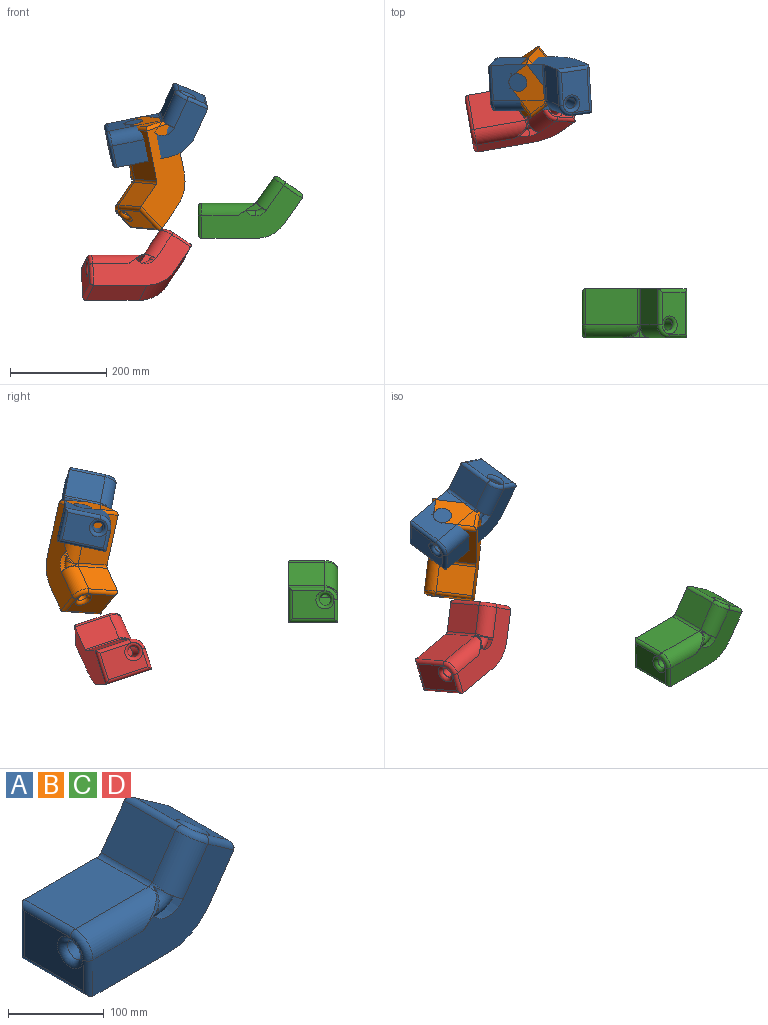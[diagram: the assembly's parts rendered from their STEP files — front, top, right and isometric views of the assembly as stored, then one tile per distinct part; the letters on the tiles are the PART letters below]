
ASSEMBLY  parts=4 mates=2
PART A: 31 faces, bbox 325x209.5x236.6 mm
  f0: plane 87.17x58.18mm, normal (-1,0,0), area 3893.8mm2, adj f23,f24,f25,f26,f27,f28
  f1: plane 313.41x215.48mm, normal (0,-1,0), area 10541.5mm2, adj f4,f5,f7,f10,f11,f13,f14,f20
  f2: plane 207.94x125.13mm, normal (0,1,0), area 15339.8mm2, adj f3,f4,f10,f12,f14,f21,f25,f29
  f3: plane 107.82x75.52mm, normal (0,0,1), area 8141.8mm2, adj f2,f5,f27,f29
  f4: plane 111.65x101.88mm, normal (0,0,-1), area 11375.1mm2, adj f1,f2,f10,f24
  f5: cylinder r=26.37mm len=109.04mm, axis (-1,0,0), area 3957.5mm2, adj f1,f3,f11,f28,f30
  f6: cylinder r=11.35mm len=111.65mm, axis (1,0,0), area 5963.8mm2, adj f8,f9,f23
  f7: torus R=26.37mm, axis (0,1,0), area 26428.1mm2, adj f1,f11,f13,f30
  f8: torus R=26.37mm, axis (0,1,0), area 2741.6mm2, adj f6,f9,f15
  f9: plane 27.05x23.34mm, normal (-0.57,0,0.82), area 564.2mm2, adj f6,f8
  f10: cylinder r=72.9mm len=101.88mm, axis (0,1,0), area 7129.5mm2, adj f1,f2,f4,f14
  f11: plane 44.36x33.31mm, normal (-0.57,0,0.82), area 108.7mm2, adj f1,f5,f7,f30
  f12: plane 75.52x49.09mm, normal (-0.82,0,0.57), area 4525.7mm2, adj f2,f13,f19,f29
  f13: cylinder r=26.37mm len=67.35mm, axis (-0.57,0,-0.82), area 2606.9mm2, adj f1,f7,f12,f18,f30
  f14: plane 101.88x52.23mm, normal (0.82,0,-0.57), area 6496.2mm2, adj f1,f2,f10,f22
  f15: cylinder r=11.35mm len=65.25mm, axis (-0.57,0,-0.82), area 4548.5mm2, adj f8,f17
  f16: plane 87.17x47.66mm, normal (0.57,0,0.82), area 3893.8mm2, adj f17,f18,f19,f20,f21,f22
  f17: torus R=18.71mm, axis (-0.57,0,-0.82), area 1018.8mm2, adj f15,f16
  f18: torus R=19.01mm, axis (-0.57,0,-0.82), area 430.2mm2, adj f13,f16,f19,f20
  f19: cylinder r=7.36mm len=75.52mm, axis (0,-1,0), area 830.3mm2, adj f12,f16,f18,f21
  f20: cylinder r=7.36mm len=42.34mm, axis (0.82,0,-0.57), area 495.3mm2, adj f1,f16,f18,f22
  f21: cylinder r=7.36mm len=63.94mm, axis (-0.82,0,0.57), area 757.6mm2, adj f2,f16,f19,f22
  f22: cylinder r=7.36mm len=101.88mm, axis (0,1,0), area 1092.6mm2, adj f14,f16,f20,f21
  f23: torus R=18.71mm, axis (-1,0,0), area 1018.8mm2, adj f0,f6
  f24: cylinder r=7.36mm len=101.88mm, axis (0,-1,0), area 1092.6mm2, adj f0,f4,f25,f26
  f25: cylinder r=7.36mm len=72.9mm, axis (0,0,-1), area 757.6mm2, adj f0,f2,f24,f27
  f26: cylinder r=7.36mm len=46.53mm, axis (0,0,1), area 495.3mm2, adj f0,f1,f24,f28
  f27: cylinder r=7.36mm len=75.52mm, axis (0,1,0), area 830.3mm2, adj f0,f3,f25,f28
  f28: torus R=19.01mm, axis (-1,0,0), area 430.2mm2, adj f0,f5,f26,f27
  f29: cylinder r=7.36mm len=75.52mm, axis (0,-1,0), area 533.4mm2, adj f2,f3,f12,f30
  f30: bspline ~20.84x9.67mm, area 64.4mm2, adj f5,f7,f11,f13,f29
PART B: same geometry as A
PART C: same geometry as A
PART D: same geometry as A
PLACE A rot(axis=(0.72,-0.68,0.13),16.7deg) t=(92,462.82,213.44)mm
PLACE B rot(axis=(0.76,0.28,-0.58),160.1deg) t=(133.9,322.82,107.64)mm
PLACE C t=(279.71,-16.55,6.8)mm
PLACE D rot(axis=(-0.87,-0.08,0.48),20.5deg) t=(29.49,384.5,-136.42)mm
MATE revolute A.f3 <-> B.f5  axis (-0.19,-0.21,0.96) through (-6.49,361.77,247.54)mm
MATE pin_slot B.f16 <-> D.f16  axis (-0.52,-0.35,-0.78) through (2.33,341.56,44.09)mm
